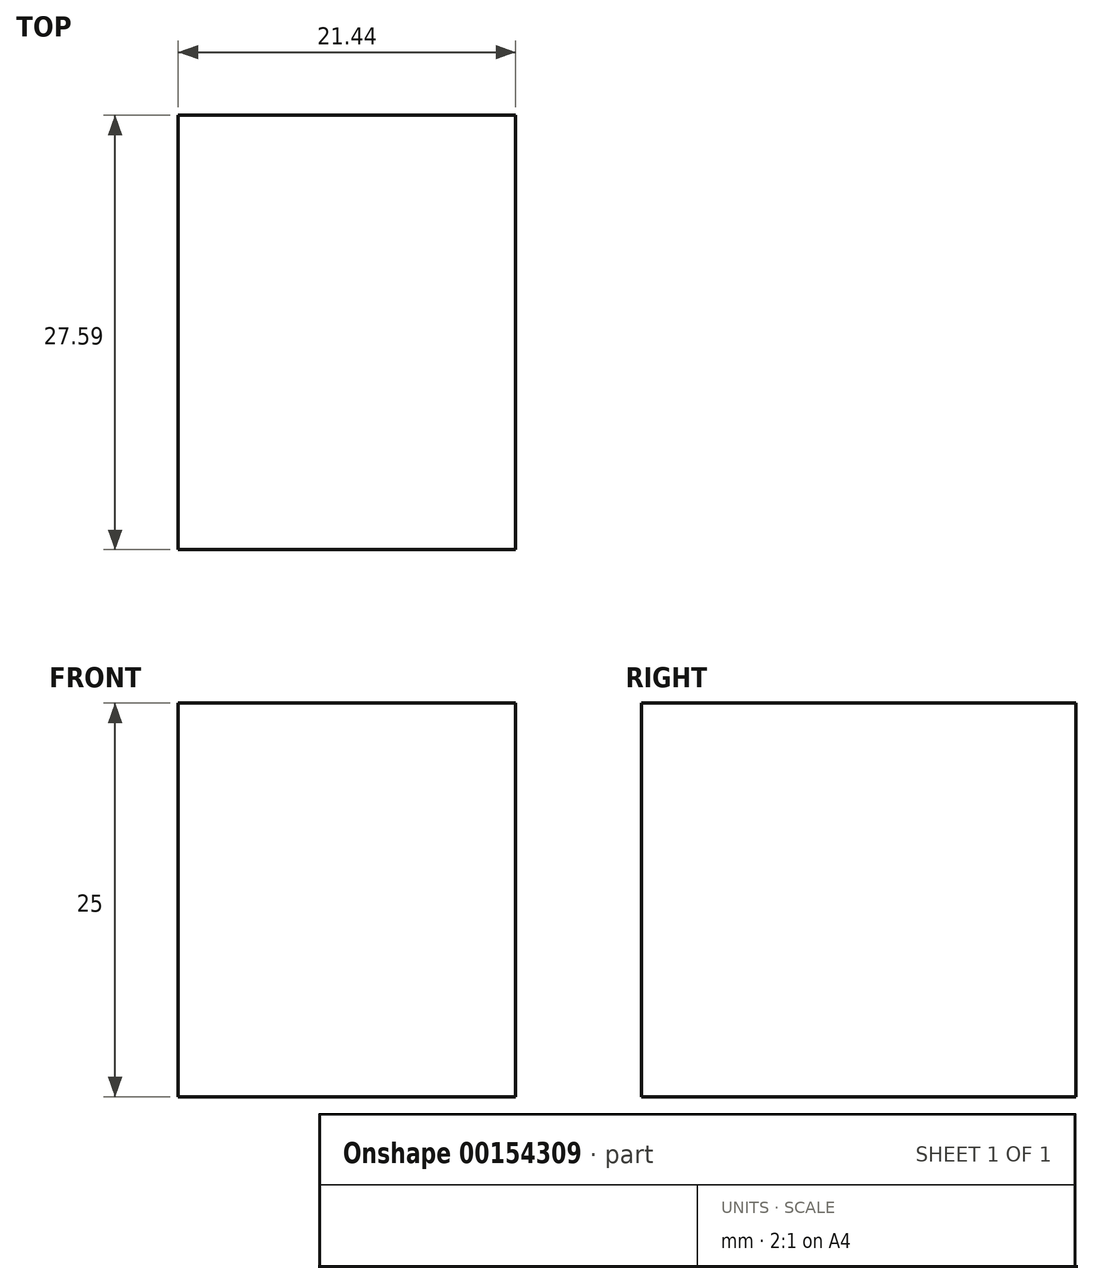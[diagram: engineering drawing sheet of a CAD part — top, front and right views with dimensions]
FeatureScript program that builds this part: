
annotation { "Feature Type Name" : "Feature", "Feature Type Description" : "" }
export const myFeature = defineFeature(function(context is Context, id is Id, definition is map)
    precondition{}
    {
        {
            var Q0;
            Q0=qCreatedBy(makeId("Top.planeOp"),FACE);
            var sketch = newSketch(context, id + "F0", { "sketchPlane" : qUnion([Q0])});
            skLineSegment(sketch, "E0.bottom", {"start": v(0, 0) * mm, "end": v(21.44, 0) * mm});
            skLineSegment(sketch, "E0.top", {"start": v(0, 27.59) * mm, "end": v(21.44, 27.59) * mm});
            skLineSegment(sketch, "E0.left", {"start": v(0, 0) * mm, "end": v(0, 27.59) * mm});
            skLineSegment(sketch, "E0.right", {"start": v(21.44, 0) * mm, "end": v(21.44, 27.59) * mm});
            skSolve(sketch);
        }
        {
            var Q0;
            Q0 = qSketchRegion(id + "F0", true);
            extrude(context, id + "F1", {"entities" : qUnion([Q0]), "depth" : 25 * mm});
        }
    });
